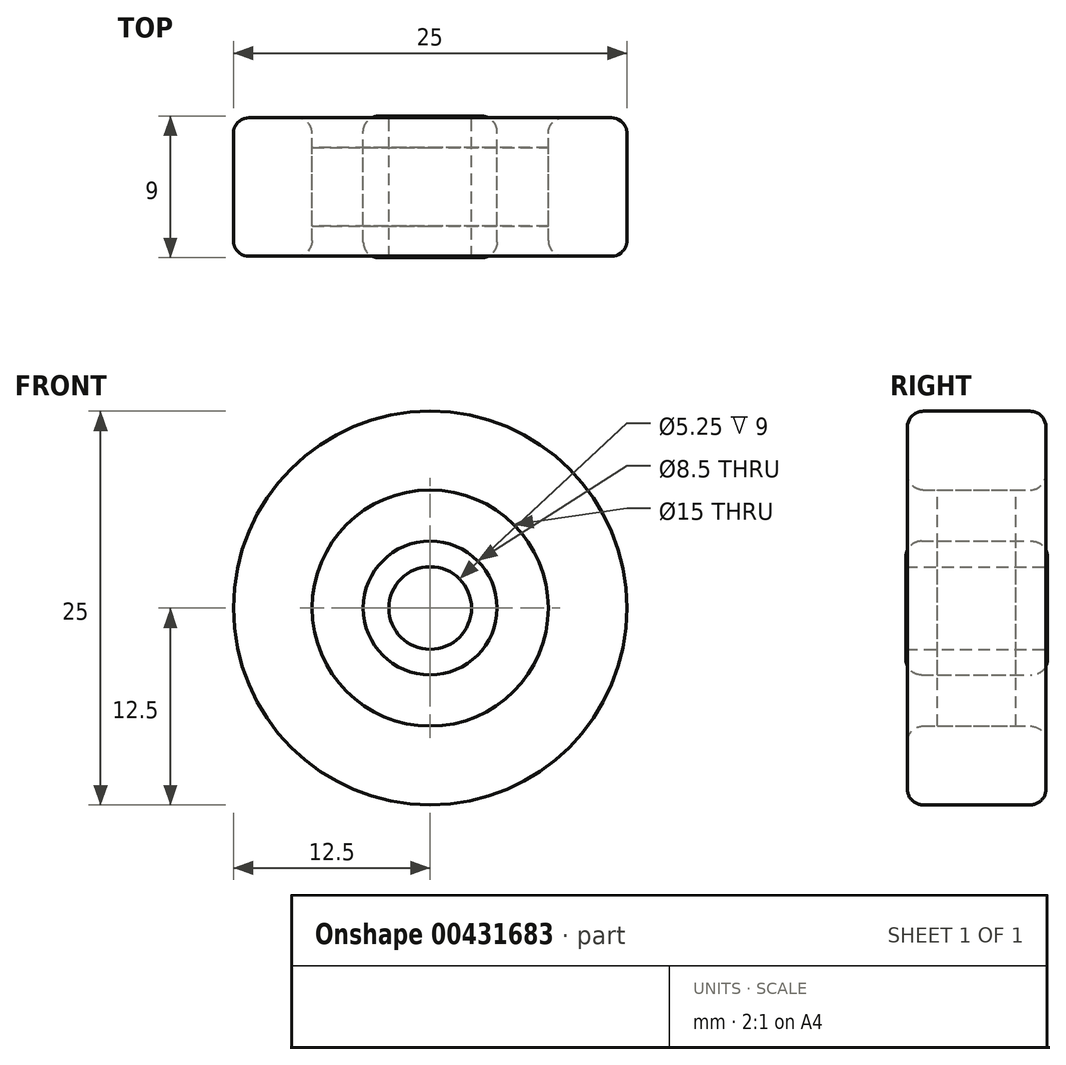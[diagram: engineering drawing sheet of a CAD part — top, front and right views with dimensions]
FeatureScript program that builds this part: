
annotation { "Feature Type Name" : "Feature", "Feature Type Description" : "" }
export const myFeature = defineFeature(function(context is Context, id is Id, definition is map)
    precondition{}
    {
        {
            var Q0;
            Q0=qCreatedBy(makeId("Front.planeOp"),FACE);
            var sketch = newSketch(context, id + "F0", { "sketchPlane" : qUnion([Q0])});
            skCircle(sketch, "E0", {"center": v(0, 0) * mm, "radius": 12.5 * mm});
            skCircle(sketch, "E1", {"center": v(0, 0) * mm, "radius": 7.5 * mm});
            skCircle(sketch, "E2", {"center": v(0, 0) * mm, "radius": 4.25 * mm});
            skCircle(sketch, "E3", {"center": v(0, 0) * mm, "radius": 2.62 * mm});
            skSolve(sketch);
        }
        {
            var Q0;
            Q0=makeQuery(id+"F0.imprint","IMPRINT",FACE,{"disambiguationData":[TD([[makeQuery(id+"F0.imprint","IMPRINT",EDGE,{"derivedFrom":sQuery(id+"F0.wireOp",EDGE,"E0")}),1.0]])]});
            extrude(context, id + "F1", {"entities" : qUnion([Q0]), "depth" : 8.8 * mm, "symmetric" : true});
        }
        {
            var Q0;
            Q0=makeQuery(id+"F0.imprint","IMPRINT",FACE,{"disambiguationData":[TD([[makeQuery(id+"F0.imprint","IMPRINT",EDGE,{"derivedFrom":sQuery(id+"F0.wireOp",EDGE,"E2")}),1.0]])]});
            extrude(context, id + "F2", {"entities" : qUnion([Q0]), "depth" : 9 * mm, "symmetric" : true});
        }
        {
            var Q0;
            Q0=makeQuery(id+"F0.imprint","IMPRINT",FACE,{"disambiguationData":[TD([[makeQuery(id+"F0.imprint","IMPRINT",EDGE,{"derivedFrom":sQuery(id+"F0.wireOp",EDGE,"E1")}),1.0]])]});
            extrude(context, id + "F3", {"entities" : qUnion([Q0]), "depth" : 5 * mm, "symmetric" : true});
        }
        {
            var Q0;
            Q0=makeQuery(id+"F2.opExtrude","CAP_EDGE",EDGE,{"disambiguationData":[OSD([sQuery(id+"F0.wireOp",EDGE,"E2")])],"isStart":false});
            var Q1;
            Q1=makeQuery(id+"F1.opExtrude","CAP_EDGE",EDGE,{"disambiguationData":[OSD([sQuery(id+"F0.wireOp",EDGE,"E1")])],"isStart":false});
            var Q2;
            Q2=makeQuery(id+"F1.opExtrude","CAP_EDGE",EDGE,{"disambiguationData":[OSD([sQuery(id+"F0.wireOp",EDGE,"E0")])],"isStart":false});
            var Q3;
            Q3=makeQuery(id+"F2.opExtrude","CAP_EDGE",EDGE,{"disambiguationData":[OSD([sQuery(id+"F0.wireOp",EDGE,"E2")])],"isStart":true});
            var Q4;
            Q4=makeQuery(id+"F1.opExtrude","CAP_EDGE",EDGE,{"disambiguationData":[OSD([sQuery(id+"F0.wireOp",EDGE,"E1")])],"isStart":true});
            var Q5;
            Q5=makeQuery(id+"F1.opExtrude","CAP_EDGE",EDGE,{"disambiguationData":[OSD([sQuery(id+"F0.wireOp",EDGE,"E0")])],"isStart":true});
            fillet(context, id + "F4", {"entities" : qUnion([Q0, Q1, Q2, Q3, Q4, Q5]), "radius" : 1 * mm, "tangentPropagation" : true, "allowEdgeOverflow" : false});
        }
    });
